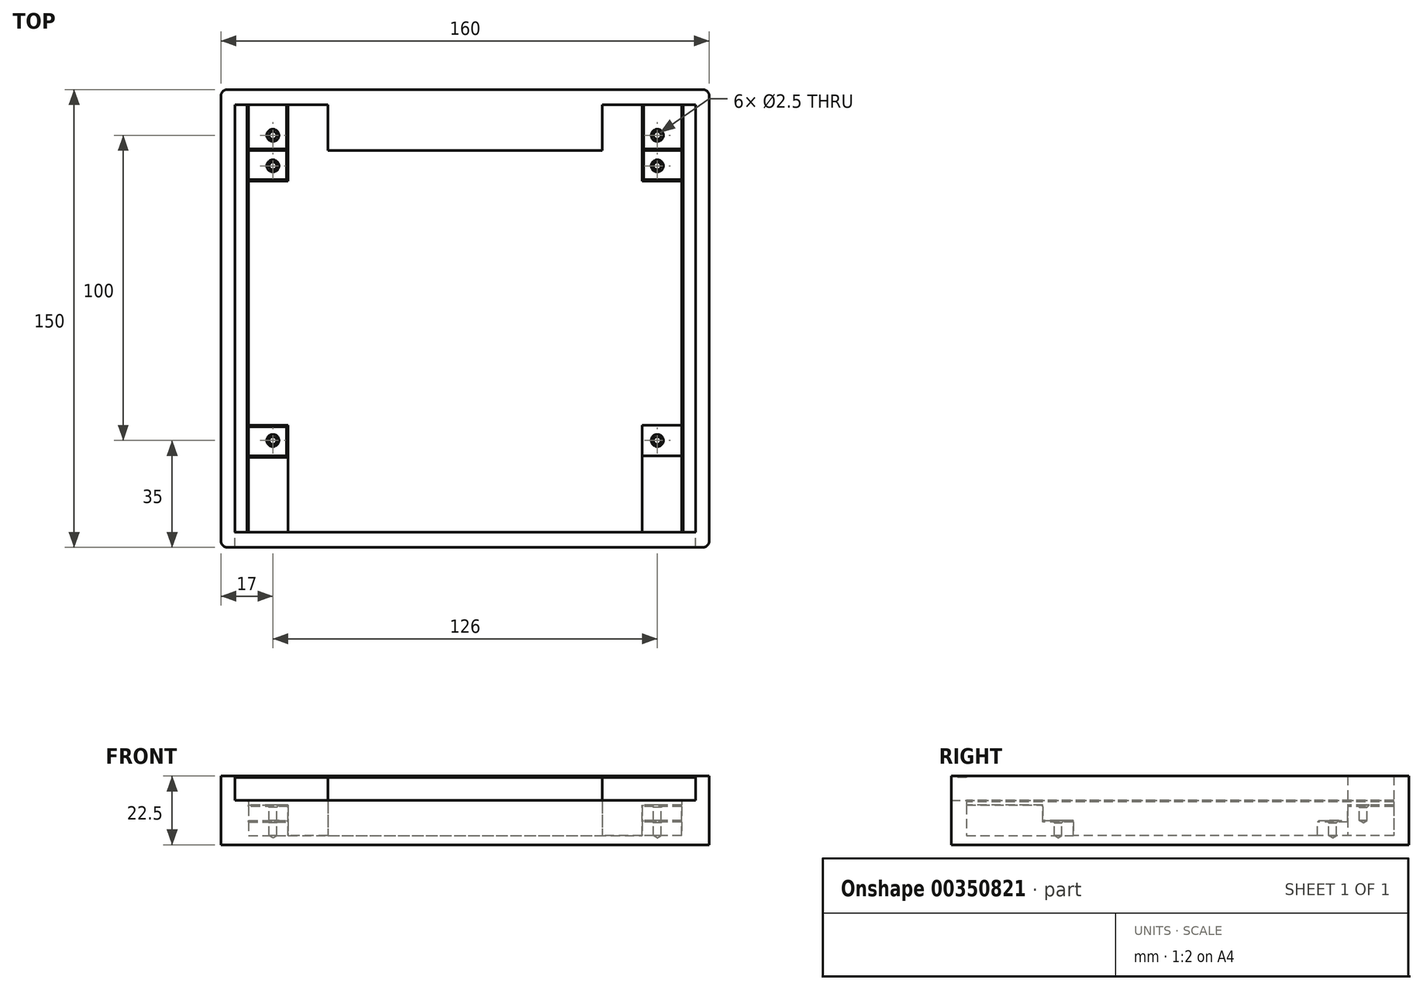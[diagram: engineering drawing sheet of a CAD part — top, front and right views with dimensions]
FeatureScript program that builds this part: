
annotation { "Feature Type Name" : "Feature", "Feature Type Description" : "" }
export const myFeature = defineFeature(function(context is Context, id is Id, definition is map)
    precondition{}
    {
        {
            var Q0;
            Q0=qCreatedBy(makeId("Top.planeOp"),FACE);
            var sketch = newSketch(context, id + "F0", { "sketchPlane" : qUnion([Q0])});
            skLineSegment(sketch, "E0.bottom", {"start": v(78, -75) * mm, "end": v(-78, -75) * mm});
            skLineSegment(sketch, "E0.top", {"start": v(78, 75) * mm, "end": v(-78, 75) * mm});
            skLineSegment(sketch, "E0.left", {"start": v(80, -73) * mm, "end": v(80, 73) * mm});
            skLineSegment(sketch, "E0.right", {"start": v(-80, -73) * mm, "end": v(-80, 73) * mm});
            skPoint(sketch, "E0.middle", {"position": v(0, 0) * mm});
            skPoint(sketch, "E1.visualSharp", {"position": v(-80, 75) * mm});
            skArc(sketch, "E1.filletArc", {"start": v(-78, 75) * mm, "mid": v(-79.41, 74.41) * mm, "end": v(-80, 73) * mm});
            skPoint(sketch, "E2.visualSharp", {"position": v(80, 75) * mm});
            skArc(sketch, "E2.filletArc", {"start": v(80, 73) * mm, "mid": v(79.41, 74.41) * mm, "end": v(78, 75) * mm});
            skPoint(sketch, "E3.visualSharp", {"position": v(80, -75) * mm});
            skArc(sketch, "E3.filletArc", {"start": v(78, -75) * mm, "mid": v(79.41, -74.41) * mm, "end": v(80, -73) * mm});
            skPoint(sketch, "E4.visualSharp", {"position": v(-80, -75) * mm});
            skArc(sketch, "E4.filletArc", {"start": v(-80, -73) * mm, "mid": v(-79.41, -74.41) * mm, "end": v(-78, -75) * mm});
            skSolve(sketch);
        }
        {
            var Q0;
            Q0 = qSketchRegion(id + "F0", true);
            extrude(context, id + "F1", {"entities" : qUnion([Q0]), "depth" : 3 * mm});
        }
        {
            var Q0;
            Q0=makeQuery(id+"F1.opExtrude","CAP_FACE",FACE,{"disambiguationData":[OSD([sQuery(id+"F0.wireOp",EDGE,"E0.bottom"),sQuery(id+"F0.wireOp",EDGE,"E0.top"),sQuery(id+"F0.wireOp",EDGE,"E0.left"),sQuery(id+"F0.wireOp",EDGE,"E0.right"),sQuery(id+"F0.wireOp",EDGE,"E1.filletArc"),sQuery(id+"F0.wireOp",EDGE,"E2.filletArc"),sQuery(id+"F0.wireOp",EDGE,"E3.filletArc"),sQuery(id+"F0.wireOp",EDGE,"E4.filletArc")])],"isStart":false});
            var sketch = newSketch(context, id + "F2", { "sketchPlane" : qUnion([Q0])});
            skLineSegment(sketch, "E5", {"start": v(15.36, 0) * mm, "end": v(-11.97, 0) * mm, "construction": true});
            skLineSegment(sketch, "E6", {"start": v(0, -7.28) * mm, "end": v(0, 8.54) * mm, "construction": true});
            skLineSegment(sketch, "E7.bottom", {"start": v(-68, -45) * mm, "end": v(-58, -45) * mm});
            skLineSegment(sketch, "E7.top", {"start": v(-68, -35) * mm, "end": v(-58, -35) * mm});
            skLineSegment(sketch, "E7.left", {"start": v(-68, -45) * mm, "end": v(-68, -35) * mm});
            skLineSegment(sketch, "E7.right", {"start": v(-58, -45) * mm, "end": v(-58, -35) * mm});
            skLineSegment(sketch, "E8.bottom", {"start": v(-68, 55) * mm, "end": v(-58, 55) * mm});
            skLineSegment(sketch, "E8.top", {"start": v(-68, 45) * mm, "end": v(-58, 45) * mm});
            skLineSegment(sketch, "E8.left", {"start": v(-68, 55) * mm, "end": v(-68, 45) * mm});
            skLineSegment(sketch, "E8.right", {"start": v(-58, 55) * mm, "end": v(-58, 45) * mm});
            skLineSegment(sketch, "E9.MirrorCS", {"start": v(68, 55) * mm, "end": v(68, 45) * mm});
            skLineSegment(sketch, "E10.MirrorCS", {"start": v(58, -45) * mm, "end": v(58, -35) * mm});
            skLineSegment(sketch, "E11.MirrorCS", {"start": v(68, -35) * mm, "end": v(58, -35) * mm});
            skLineSegment(sketch, "E12.MirrorCS", {"start": v(58, 55) * mm, "end": v(58, 45) * mm});
            skLineSegment(sketch, "E13.MirrorCS", {"start": v(68, -45) * mm, "end": v(68, -35) * mm});
            skLineSegment(sketch, "E14.MirrorCS", {"start": v(68, 55) * mm, "end": v(58, 55) * mm});
            skLineSegment(sketch, "E15.MirrorCS", {"start": v(68, 45) * mm, "end": v(58, 45) * mm});
            skLineSegment(sketch, "E16.MirrorCS", {"start": v(68, -45) * mm, "end": v(58, -45) * mm});
            skSolve(sketch);
        }
        {
            var Q0;
            Q0 = qSketchRegion(id + "F2", true);
            extrude(context, id + "F3", {"entities" : qUnion([Q0]), "operationType" : NewBodyOperationType.ADD, "depth" : 5 * mm});
        }
        {
            var Q0;
            Q0=makeQuery(id+"F3.opExtrude","CAP_FACE",FACE,{"disambiguationData":[OSD([sQuery(id+"F2.wireOp",EDGE,"E8.bottom"),sQuery(id+"F2.wireOp",EDGE,"E8.top"),sQuery(id+"F2.wireOp",EDGE,"E8.left"),sQuery(id+"F2.wireOp",EDGE,"E8.right")])],"isStart":false});
            var sketch = newSketch(context, id + "F4", { "sketchPlane" : qUnion([Q0])});
            skLineSegment(sketch, "E17", {"start": v(0, 12.76) * mm, "end": v(0, -16.1) * mm, "construction": true});
            skLineSegment(sketch, "E18", {"start": v(-10.9, 0) * mm, "end": v(16.66, 0) * mm, "construction": true});
            skPoint(sketch, "E19", {"position": v(-63, 50) * mm});
            skPoint(sketch, "E19.positionSnap0", {"position": v(-63, 55) * mm});
            skPoint(sketch, "E19.positionSnap1", {"position": v(-58, 50) * mm});
            skPoint(sketch, "E20", {"position": v(-63, -40) * mm});
            skPoint(sketch, "E21.MirrorP", {"position": v(63, -40) * mm});
            skPoint(sketch, "E22.MirrorP", {"position": v(58, 50) * mm});
            skPoint(sketch, "E23.MirrorP", {"position": v(63, 50) * mm});
            skSolve(sketch);
        }
        {
            var Q0;
            Q0=makeQuery(id+"F1.opExtrude","CAP_FACE",FACE,{"disambiguationData":[OSD([sQuery(id+"F0.wireOp",EDGE,"E0.bottom"),sQuery(id+"F0.wireOp",EDGE,"E0.top"),sQuery(id+"F0.wireOp",EDGE,"E0.left"),sQuery(id+"F0.wireOp",EDGE,"E0.right"),sQuery(id+"F0.wireOp",EDGE,"E1.filletArc"),sQuery(id+"F0.wireOp",EDGE,"E2.filletArc"),sQuery(id+"F0.wireOp",EDGE,"E3.filletArc"),sQuery(id+"F0.wireOp",EDGE,"E4.filletArc")])],"isStart":false});
            var sketch = newSketch(context, id + "F5", { "sketchPlane" : qUnion([Q0])});
            skLineSegment(sketch, "E24.bottom", {"start": v(-68, 55) * mm, "end": v(-58, 55) * mm});
            skLineSegment(sketch, "E24.top", {"start": v(-68, 65) * mm, "end": v(-58, 65) * mm});
            skLineSegment(sketch, "E24.left", {"start": v(-68, 55) * mm, "end": v(-68, 65) * mm});
            skLineSegment(sketch, "E24.right", {"start": v(-58, 55) * mm, "end": v(-58, 65) * mm});
            skLineSegment(sketch, "E25", {"start": v(0, -3.53) * mm, "end": v(0, 31.26) * mm, "construction": true});
            skLineSegment(sketch, "E26", {"start": v(-9.48, 0) * mm, "end": v(18.02, 0) * mm, "construction": true});
            skLineSegment(sketch, "E27.bottom", {"start": v(-68, -45) * mm, "end": v(-58, -45) * mm});
            skLineSegment(sketch, "E27.top", {"start": v(-68, -55) * mm, "end": v(-58, -55) * mm});
            skLineSegment(sketch, "E27.left", {"start": v(-68, -45) * mm, "end": v(-68, -55) * mm});
            skLineSegment(sketch, "E27.right", {"start": v(-58, -45) * mm, "end": v(-58, -55) * mm});
            skLineSegment(sketch, "E28.MirrorCS", {"start": v(68, 55) * mm, "end": v(58, 55) * mm});
            skLineSegment(sketch, "E29.MirrorCS", {"start": v(68, 65) * mm, "end": v(58, 65) * mm});
            skLineSegment(sketch, "E30.MirrorCS", {"start": v(68, -55) * mm, "end": v(58, -55) * mm});
            skLineSegment(sketch, "E31.MirrorCS", {"start": v(58, 55) * mm, "end": v(58, 65) * mm});
            skLineSegment(sketch, "E32.MirrorCS", {"start": v(58, -45) * mm, "end": v(58, -55) * mm});
            skLineSegment(sketch, "E33.MirrorCS", {"start": v(68, -45) * mm, "end": v(68, -55) * mm});
            skLineSegment(sketch, "E34.MirrorCS", {"start": v(68, -45) * mm, "end": v(58, -45) * mm});
            skLineSegment(sketch, "E35.MirrorCS", {"start": v(68, 55) * mm, "end": v(68, 65) * mm});
            skSolve(sketch);
        }
        {
            var Q0;
            Q0 = qSketchRegion(id + "F5", true);
            extrude(context, id + "F6", {"entities" : qUnion([Q0]), "operationType" : NewBodyOperationType.ADD, "depth" : 10 * mm});
        }
        {
            var Q0;
            Q0=makeQuery(id+"F6.opExtrude","CAP_FACE",FACE,{"disambiguationData":[OSD([sQuery(id+"F5.wireOp",EDGE,"E24.bottom"),sQuery(id+"F5.wireOp",EDGE,"E24.top"),sQuery(id+"F5.wireOp",EDGE,"E24.left"),sQuery(id+"F5.wireOp",EDGE,"E24.right")])],"isStart":false});
            var sketch = newSketch(context, id + "F7", { "sketchPlane" : qUnion([Q0])});
            skPoint(sketch, "E36", {"position": v(-63, 60) * mm});
            skPoint(sketch, "E36.positionSnap0", {"position": v(-58, 60) * mm});
            skPoint(sketch, "E37", {"position": v(63, 60) * mm});
            skSolve(sketch);
        }
        {
            var Q0;
            Q0=sQuery(id+"F4.wireOp",VERTEX,"dee3a072-0559-4f3e-aa8e-34885224e21b");
            var Q1;
            Q1=sQuery(id+"F4.wireOp",VERTEX,"d39e51ca-cc14-4291-bc97-98dbb002058f0.MirrorP");
            var Q2;
            Q2=sQuery(id+"F4.wireOp",VERTEX,"d39e51ca-cc14-4291-bc97-98dbb002058f1.MirrorP");
            var Q3;
            Q3=sQuery(id+"F4.wireOp",VERTEX,"049a6676-49f8-4cd7-b6db-b765b2aac7f50.MirrorP");
            var Q4;
            Q4=sQuery(id+"F7.wireOp",VERTEX,"E36");
            var Q5;
            Q5=sQuery(id+"F7.wireOp",VERTEX,"E37");
            var Q6;
            Q6=sQuery(id+"F4.wireOp",VERTEX,"E20");
            var Q7;
            Q7=sQuery(id+"F4.wireOp",VERTEX,"E21.MirrorP");
            var Q8;
            Q8=sQuery(id+"F4.wireOp",VERTEX,"E19");
            var Q9;
            Q9=sQuery(id+"F4.wireOp",VERTEX,"E23.MirrorP");
            var Q10;
            Q10=makeQuery(id+"F1.opExtrude","SWEPT_BODY",BODY,{"disambiguationData":[OSD([sQuery(id+"F0.wireOp",EDGE,"E0.bottom"),sQuery(id+"F0.wireOp",EDGE,"E0.top"),sQuery(id+"F0.wireOp",EDGE,"E0.left"),sQuery(id+"F0.wireOp",EDGE,"E0.right"),sQuery(id+"F0.wireOp",EDGE,"E1.filletArc"),sQuery(id+"F0.wireOp",EDGE,"E2.filletArc"),sQuery(id+"F0.wireOp",EDGE,"E3.filletArc"),sQuery(id+"F0.wireOp",EDGE,"E4.filletArc")])]});
            hole(context, id + "F8", {"style" : HoleStyle.C_SINK, "endStyle" : HoleEndStyle.BLIND, "holeDiameter" : 2.5 * mm, "cSinkDiameter" : 4 * mm, "cSinkAngle" : 90 * degree, "holeDepth" : 5 * mm, "isTappedThrough" : true, "tappedDepth" : 5 * mm, "tapClearance" : 3, "locations" : qUnion([Q0, Q1, Q2, Q3, Q4, Q5, Q6, Q7, Q8, Q9]), "scope" : qUnion([Q10])});
        }
        {
            var Q0;
            Q0=makeQuery(id+"F1.opExtrude","CAP_FACE",FACE,{"disambiguationData":[OSD([sQuery(id+"F0.wireOp",EDGE,"E0.bottom"),sQuery(id+"F0.wireOp",EDGE,"E0.top"),sQuery(id+"F0.wireOp",EDGE,"E0.left"),sQuery(id+"F0.wireOp",EDGE,"E0.right"),sQuery(id+"F0.wireOp",EDGE,"E1.filletArc"),sQuery(id+"F0.wireOp",EDGE,"E2.filletArc"),sQuery(id+"F0.wireOp",EDGE,"E3.filletArc"),sQuery(id+"F0.wireOp",EDGE,"E4.filletArc")])],"isStart":false});
            var sketch = newSketch(context, id + "F9", { "sketchPlane" : qUnion([Q0])});
            skLineSegment(sketch, "E38.top", {"start": v(-71, -70) * mm, "end": v(-80, -70) * mm});
            skLineSegment(sketch, "E38.left", {"start": v(-71, 70) * mm, "end": v(-71, -70) * mm});
            skLineSegment(sketch, "E38.right", {"start": v(-80, 70) * mm, "end": v(-80, -70) * mm});
            skLineSegment(sketch, "E39", {"start": v(0, -8.37) * mm, "end": v(0, 11.77) * mm, "construction": true});
            skLineSegment(sketch, "E40.MirrorCS", {"start": v(80, 70) * mm, "end": v(80, -70) * mm});
            skLineSegment(sketch, "E41.MirrorCS", {"start": v(71, 70) * mm, "end": v(71, -70) * mm});
            skLineSegment(sketch, "E42.MirrorCS", {"start": v(71, -70) * mm, "end": v(80, -70) * mm});
            skLineSegment(sketch, "E43", {"start": v(-80, 70) * mm, "end": v(-71, 70) * mm});
            skLineSegment(sketch, "E44", {"start": v(71, 70) * mm, "end": v(80, 70) * mm});
            skSolve(sketch);
        }
        {
            var Q0;
            Q0 = qSketchRegion(id + "F9", true);
            extrude(context, id + "F10", {"entities" : qUnion([Q0]), "operationType" : NewBodyOperationType.ADD, "depth" : 11.5 * mm});
        }
        {
            var Q0;
            Q0=makeQuery(id+"F10.opExtrude","CAP_FACE",FACE,{"disambiguationData":[OSD([sQuery(id+"F9.wireOp",EDGE,"E38.bottom"),sQuery(id+"F9.wireOp",EDGE,"E38.top"),sQuery(id+"F9.wireOp",EDGE,"E38.left"),sQuery(id+"F9.wireOp",EDGE,"E38.right")])],"isStart":false});
            var sketch = newSketch(context, id + "F11", { "sketchPlane" : qUnion([Q0])});
            skLineSegment(sketch, "E45.bottom", {"start": v(-80, -70) * mm, "end": v(-75.5, -70) * mm});
            skLineSegment(sketch, "E45.top", {"start": v(-80, -70) * mm, "end": v(-75.5, -70) * mm});
            skLineSegment(sketch, "E45.left", {"start": v(-80, -70) * mm, "end": v(-80, -70) * mm});
            skLineSegment(sketch, "E45.right", {"start": v(-75.5, -70) * mm, "end": v(-75.5, -70) * mm});
            skLineSegment(sketch, "E46", {"start": v(0, -3.83) * mm, "end": v(0, 7.5) * mm, "construction": true});
            skLineSegment(sketch, "E47.MirrorCS", {"start": v(75.5, -70) * mm, "end": v(75.5, -70) * mm});
            skLineSegment(sketch, "E48.MirrorCS", {"start": v(80, -70) * mm, "end": v(80, -70) * mm});
            skLineSegment(sketch, "E49.MirrorCS", {"start": v(80, -70) * mm, "end": v(75.5, -70) * mm});
            skLineSegment(sketch, "E50", {"start": v(-75.5, -70) * mm, "end": v(-75.5, 70) * mm});
            skLineSegment(sketch, "E51", {"start": v(-75.5, 70) * mm, "end": v(-80, 70) * mm});
            skLineSegment(sketch, "E52", {"start": v(-80, 70) * mm, "end": v(-80, -70) * mm});
            skLineSegment(sketch, "E53.MirrorCS", {"start": v(75.5, 70) * mm, "end": v(80, 70) * mm});
            skLineSegment(sketch, "E54.MirrorCS", {"start": v(75.5, -70) * mm, "end": v(75.5, 70) * mm});
            skLineSegment(sketch, "E55.0", {"start": v(80, -70) * mm, "end": v(80, 70) * mm});
            skSolve(sketch);
        }
        {
            var Q0;
            Q0 = qSketchRegion(id + "F11", true);
            extrude(context, id + "F12", {"entities" : qUnion([Q0]), "operationType" : NewBodyOperationType.ADD, "depth" : 8 * mm});
        }
        {
            var Q0;
            Q0=makeQuery(id+"F1.opExtrude","CAP_FACE",FACE,{"disambiguationData":[OSD([sQuery(id+"F0.wireOp",EDGE,"E0.bottom"),sQuery(id+"F0.wireOp",EDGE,"E0.top"),sQuery(id+"F0.wireOp",EDGE,"E0.left"),sQuery(id+"F0.wireOp",EDGE,"E0.right"),sQuery(id+"F0.wireOp",EDGE,"E1.filletArc"),sQuery(id+"F0.wireOp",EDGE,"E2.filletArc"),sQuery(id+"F0.wireOp",EDGE,"E3.filletArc"),sQuery(id+"F0.wireOp",EDGE,"E4.filletArc")])],"isStart":false});
            var sketch = newSketch(context, id + "F13", { "sketchPlane" : qUnion([Q0])});
            skLineSegment(sketch, "E56.0", {"start": v(-80, -73) * mm, "end": v(-80, -70) * mm});
            skArc(sketch, "E56.1", {"start": v(-80, -73) * mm, "mid": v(-79.41, -74.41) * mm, "end": v(-78, -75) * mm});
            skLineSegment(sketch, "E56.2", {"start": v(78, -75) * mm, "end": v(-78, -75) * mm});
            skArc(sketch, "E56.3", {"start": v(78, -75) * mm, "mid": v(79.41, -74.41) * mm, "end": v(80, -73) * mm});
            skLineSegment(sketch, "E56.4", {"start": v(80, -73) * mm, "end": v(80, -70) * mm});
            skLineSegment(sketch, "E57", {"start": v(-80, -70) * mm, "end": v(80, -70) * mm});
            skLineSegment(sketch, "E58.0", {"start": v(-80, 70) * mm, "end": v(-80, 73) * mm});
            skArc(sketch, "E58.1", {"start": v(-78, 75) * mm, "mid": v(-79.41, 74.41) * mm, "end": v(-80, 73) * mm});
            skLineSegment(sketch, "E58.2", {"start": v(78, 75) * mm, "end": v(-78, 75) * mm});
            skArc(sketch, "E58.3", {"start": v(80, 73) * mm, "mid": v(79.41, 74.41) * mm, "end": v(78, 75) * mm});
            skLineSegment(sketch, "E58.4", {"start": v(80, 70) * mm, "end": v(80, 73) * mm});
            skLineSegment(sketch, "E59", {"start": v(80, 70) * mm, "end": v(-80, 70) * mm});
            skSolve(sketch);
        }
        {
            var Q0;
            Q0 = qSketchRegion(id + "F13", true);
            var Q1;
            Q1=makeQuery(id+"F12.opExtrude","CAP_FACE",FACE,{"disambiguationData":[OSD([sQuery(id+"F11.wireOp",EDGE,"E45.bottom"),sQuery(id+"F11.wireOp",EDGE,"E45.top"),sQuery(id+"F11.wireOp",EDGE,"E45.left"),sQuery(id+"F11.wireOp",EDGE,"E45.right")])],"isStart":false});
            extrude(context, id + "F14", {"entities" : qUnion([Q0]), "operationType" : NewBodyOperationType.ADD, "endBound" : BoundingType.UP_TO_SURFACE, "endBoundEntityFace" : qUnion([Q1]), "depth" : 25 * mm});
        }
        {
            var Q0;
            Q0=makeQuery(id+"F14.boolean.opBoolean","MERGE",FACE,{"derivedFrom":[makeQuery(id+"F1.opExtrude","SWEPT_FACE",FACE,{"disambiguationData":[OSD([sQuery(id+"F0.wireOp",EDGE,"E0.bottom")])]}),makeQuery(id+"F14.opExtrude","SWEPT_FACE",FACE,{"disambiguationData":[OSD([sQuery(id+"F13.wireOp",EDGE,"E56.2")])]})]});
            var sketch = newSketch(context, id + "F15", { "sketchPlane" : qUnion([Q0])});
            skLineSegment(sketch, "E60.0", {"start": v(-75.5, 22) * mm, "end": v(-75.5, 14.5) * mm});
            skLineSegment(sketch, "E60.5", {"start": v(75.5, 22.5) * mm, "end": v(75.5, 14.5) * mm});
            skLineSegment(sketch, "E61", {"start": v(-75.5, 22) * mm, "end": v(75.5, 22) * mm});
            skPoint(sketch, "E62.orphan", {"position": v(-75.5, 22.5) * mm});
            skLineSegment(sketch, "E63.0", {"start": v(75.5, 14.5) * mm, "end": v(-75.5, 14.5) * mm});
            skSolve(sketch);
        }
        {
            var Q0;
            Q0 = qSketchRegion(id + "F15", true);
            extrude(context, id + "F16", {"entities" : qUnion([Q0]), "operationType" : NewBodyOperationType.REMOVE, "endBound" : BoundingType.UP_TO_NEXT, "oppositeDirection" : true, "depth" : 25 * mm});
        }
        {
            var Q0;
            Q0=makeQuery(id+"F6.boolean.opBoolean","MERGE",FACE,{"derivedFrom":[makeQuery(id+"F3.opExtrude","SWEPT_FACE",FACE,{"disambiguationData":[OSD([sQuery(id+"F2.wireOp",EDGE,"E8.left")])]}),makeQuery(id+"F6.opExtrude","SWEPT_FACE",FACE,{"disambiguationData":[OSD([sQuery(id+"F5.wireOp",EDGE,"E24.left")])]})]});
            var sketch = newSketch(context, id + "F17", { "sketchPlane" : qUnion([Q0])});
            skLineSegment(sketch, "E64.0.0", {"start": v(-45, 3) * mm, "end": v(-65, 3) * mm});
            skLineSegment(sketch, "E64.0.1", {"start": v(-65, 3) * mm, "end": v(-65, 13) * mm});
            skLineSegment(sketch, "E64.0.2", {"start": v(-65, 13) * mm, "end": v(-55, 13) * mm});
            skLineSegment(sketch, "E64.0.3", {"start": v(-55, 13) * mm, "end": v(-55, 8) * mm});
            skLineSegment(sketch, "E64.0.4", {"start": v(-55, 8) * mm, "end": v(-45, 8) * mm});
            skLineSegment(sketch, "E64.0.5", {"start": v(-45, 8) * mm, "end": v(-45, 3) * mm});
            skLineSegment(sketch, "E65.0.0", {"start": v(55, 3) * mm, "end": v(35, 3) * mm});
            skLineSegment(sketch, "E65.0.1", {"start": v(35, 3) * mm, "end": v(35, 8) * mm});
            skLineSegment(sketch, "E65.0.2", {"start": v(35, 8) * mm, "end": v(45, 8) * mm});
            skLineSegment(sketch, "E65.0.3", {"start": v(45, 8) * mm, "end": v(45, 13) * mm});
            skLineSegment(sketch, "E65.0.4", {"start": v(45, 13) * mm, "end": v(55, 13) * mm});
            skLineSegment(sketch, "E65.0.5", {"start": v(55, 13) * mm, "end": v(55, 3) * mm});
            skSolve(sketch);
        }
        {
            var Q0;
            Q0 = qSketchRegion(id + "F17", true);
            extrude(context, id + "F18", {"entities" : qUnion([Q0]), "operationType" : NewBodyOperationType.ADD, "endBound" : BoundingType.UP_TO_NEXT, "depth" : 25 * mm});
        }
        {
            var Q0;
            Q0=makeQuery(id+"F18.boolean.opBoolean","MERGE",FACE,{"derivedFrom":[makeQuery(id+"F6.opExtrude","SWEPT_FACE",FACE,{"disambiguationData":[OSD([sQuery(id+"F5.wireOp",EDGE,"E24.top")])]}),makeQuery(id+"F18.opExtrude","SWEPT_FACE",FACE,{"disambiguationData":[OSD([sQuery(id+"F17.wireOp",EDGE,"E64.0.1")])]})]});
            var sketch = newSketch(context, id + "F19", { "sketchPlane" : qUnion([Q0])});
            skLineSegment(sketch, "E66.0.0", {"start": v(58, 3) * mm, "end": v(71, 3) * mm});
            skLineSegment(sketch, "E66.0.1", {"start": v(71, 3) * mm, "end": v(71, 13) * mm});
            skLineSegment(sketch, "E66.0.2", {"start": v(71, 13) * mm, "end": v(58, 13) * mm});
            skLineSegment(sketch, "E66.0.3", {"start": v(58, 13) * mm, "end": v(58, 3) * mm});
            skLineSegment(sketch, "E67.0.0", {"start": v(-68, 3) * mm, "end": v(-58, 3) * mm});
            skLineSegment(sketch, "E67.0.1", {"start": v(-58, 3) * mm, "end": v(-58, 13) * mm});
            skLineSegment(sketch, "E67.0.2", {"start": v(-58, 13) * mm, "end": v(-68, 13) * mm});
            skLineSegment(sketch, "E67.0.3", {"start": v(-68, 13) * mm, "end": v(-68, 3) * mm});
            skSolve(sketch);
        }
        {
            var Q0;
            Q0 = qSketchRegion(id + "F19", true);
            extrude(context, id + "F20", {"entities" : qUnion([Q0]), "operationType" : NewBodyOperationType.ADD, "endBound" : BoundingType.UP_TO_NEXT, "depth" : 25 * mm});
        }
        {
            var Q0;
            Q0=makeQuery(id+"F20.boolean.opBoolean","MERGE",FACE,{"derivedFrom":[makeQuery(id+"F6.boolean.opBoolean","MERGE",FACE,{"derivedFrom":[makeQuery(id+"F3.opExtrude","SWEPT_FACE",FACE,{"disambiguationData":[OSD([sQuery(id+"F2.wireOp",EDGE,"E9.MirrorCS")])]}),makeQuery(id+"F6.opExtrude","SWEPT_FACE",FACE,{"disambiguationData":[OSD([sQuery(id+"F5.wireOp",EDGE,"E35.MirrorCS")])]})]}),makeQuery(id+"F20.opExtrude","SWEPT_FACE",FACE,{"disambiguationData":[OSD([sQuery(id+"F19.wireOp",EDGE,"E67.0.3")])]})]});
            var sketch = newSketch(context, id + "F21", { "sketchPlane" : qUnion([Q0])});
            skLineSegment(sketch, "E68.0.0", {"start": v(45, 3) * mm, "end": v(70, 3) * mm});
            skLineSegment(sketch, "E68.0.1", {"start": v(70, 3) * mm, "end": v(70, 13) * mm});
            skLineSegment(sketch, "E68.0.2", {"start": v(70, 13) * mm, "end": v(55, 13) * mm});
            skLineSegment(sketch, "E68.0.3", {"start": v(55, 13) * mm, "end": v(55, 8) * mm});
            skLineSegment(sketch, "E68.0.4", {"start": v(55, 8) * mm, "end": v(45, 8) * mm});
            skLineSegment(sketch, "E68.0.5", {"start": v(45, 8) * mm, "end": v(45, 3) * mm});
            skLineSegment(sketch, "E69.0.0", {"start": v(-55, 3) * mm, "end": v(-35, 3) * mm});
            skLineSegment(sketch, "E69.0.1", {"start": v(-35, 3) * mm, "end": v(-35, 8) * mm});
            skLineSegment(sketch, "E69.0.2", {"start": v(-35, 8) * mm, "end": v(-45, 8) * mm});
            skLineSegment(sketch, "E69.0.3", {"start": v(-45, 8) * mm, "end": v(-45, 13) * mm});
            skLineSegment(sketch, "E69.0.4", {"start": v(-45, 13) * mm, "end": v(-55, 13) * mm});
            skLineSegment(sketch, "E69.0.5", {"start": v(-55, 13) * mm, "end": v(-55, 3) * mm});
            skSolve(sketch);
        }
        {
            var Q0;
            Q0 = qSketchRegion(id + "F21", true);
            extrude(context, id + "F22", {"entities" : qUnion([Q0]), "operationType" : NewBodyOperationType.ADD, "endBound" : BoundingType.UP_TO_NEXT, "depth" : 25 * mm});
        }
        {
            var Q0;
            Q0=makeQuery(id+"F22.boolean.opBoolean","MERGE",FACE,{"derivedFrom":[makeQuery(id+"F6.opExtrude","SWEPT_FACE",FACE,{"disambiguationData":[OSD([sQuery(id+"F5.wireOp",EDGE,"E30.MirrorCS")])]}),makeQuery(id+"F22.opExtrude","SWEPT_FACE",FACE,{"disambiguationData":[OSD([sQuery(id+"F21.wireOp",EDGE,"E69.0.5")])]})]});
            var sketch = newSketch(context, id + "F23", { "sketchPlane" : qUnion([Q0])});
            skLineSegment(sketch, "E70.0.0", {"start": v(58, 3) * mm, "end": v(71, 3) * mm});
            skLineSegment(sketch, "E70.0.1", {"start": v(71, 3) * mm, "end": v(71, 13) * mm});
            skLineSegment(sketch, "E70.0.2", {"start": v(71, 13) * mm, "end": v(58, 13) * mm});
            skLineSegment(sketch, "E70.0.3", {"start": v(58, 13) * mm, "end": v(58, 3) * mm});
            skLineSegment(sketch, "E71.0.0", {"start": v(-71, 3) * mm, "end": v(-58, 3) * mm});
            skLineSegment(sketch, "E71.0.1", {"start": v(-58, 3) * mm, "end": v(-58, 13) * mm});
            skLineSegment(sketch, "E71.0.2", {"start": v(-58, 13) * mm, "end": v(-71, 13) * mm});
            skLineSegment(sketch, "E71.0.3", {"start": v(-71, 13) * mm, "end": v(-71, 3) * mm});
            skSolve(sketch);
        }
        {
            var Q0;
            Q0 = qSketchRegion(id + "F23", true);
            extrude(context, id + "F24", {"entities" : qUnion([Q0]), "operationType" : NewBodyOperationType.ADD, "endBound" : BoundingType.UP_TO_NEXT, "depth" : 25 * mm});
        }
        {
            var Q0;
            Q0=makeQuery(id+"F1.opExtrude","CAP_FACE",FACE,{"disambiguationData":[OSD([sQuery(id+"F0.wireOp",EDGE,"E0.bottom"),sQuery(id+"F0.wireOp",EDGE,"E0.top"),sQuery(id+"F0.wireOp",EDGE,"E0.left"),sQuery(id+"F0.wireOp",EDGE,"E0.right"),sQuery(id+"F0.wireOp",EDGE,"E1.filletArc"),sQuery(id+"F0.wireOp",EDGE,"E2.filletArc"),sQuery(id+"F0.wireOp",EDGE,"E3.filletArc"),sQuery(id+"F0.wireOp",EDGE,"E4.filletArc")])],"isStart":false});
            var sketch = newSketch(context, id + "F25", { "sketchPlane" : qUnion([Q0])});
            skLineSegment(sketch, "E72.bottom", {"start": v(-45, 70) * mm, "end": v(45, 70) * mm});
            skLineSegment(sketch, "E72.top", {"start": v(-45, 55) * mm, "end": v(45, 55) * mm});
            skLineSegment(sketch, "E72.left", {"start": v(-45, 70) * mm, "end": v(-45, 55) * mm});
            skLineSegment(sketch, "E72.right", {"start": v(45, 70) * mm, "end": v(45, 55) * mm});
            skSolve(sketch);
        }
        {
            var Q0;
            Q0 = qSketchRegion(id + "F25", true);
            var Q1;
            {var subQ0=sQuery(id+"F11.wireOp",EDGE,"E52");var subQ1=sQuery(id+"F11.wireOp",EDGE,"E51");var subQ2=sQuery(id+"F11.wireOp",EDGE,"E50");var subQ3=sQuery(id+"F11.wireOp",EDGE,"E45.top");Q1=makeQuery(id+"F14.boolean.opBoolean","MERGE",FACE,{"derivedFrom":[makeQuery(id+"F12.opExtrude","CAP_FACE",FACE,{"disambiguationData":[OSD([subQ3,subQ2,subQ1,subQ0])],"isStart":false}),makeQuery(id+"F12.opExtrude","CAP_FACE",FACE,{"disambiguationData":[OSD([sQuery(id+"F11.wireOp",EDGE,"E53.MirrorCS"),sQuery(id+"F11.wireOp",EDGE,"E54.MirrorCS"),sQuery(id+"F11.wireOp",EDGE,"E49.MirrorCS"),sQuery(id+"F11.wireOp",EDGE,"E55.0")])],"isStart":false}),makeQuery(id+"F14.opExtrude","CAP_FACE",FACE,{"disambiguationData":[OSD([subQ3,subQ2,subQ1,subQ0]),ownerDisambiguation([makeQuery(id+"F13.imprint","IMPRINT",EDGE,{"derivedFrom":sQuery(id+"F13.wireOp",EDGE,"E56.0")})])],"isStart":false}),makeQuery(id+"F14.opExtrude","CAP_FACE",FACE,{"disambiguationData":[OSD([subQ3,subQ2,subQ1,subQ0]),ownerDisambiguation([makeQuery(id+"F13.imprint","IMPRINT",EDGE,{"derivedFrom":sQuery(id+"F13.wireOp",EDGE,"E58.0")})])],"isStart":false})]});}
            extrude(context, id + "F26", {"entities" : qUnion([Q0]), "operationType" : NewBodyOperationType.ADD, "endBound" : BoundingType.UP_TO_SURFACE, "endBoundEntityFace" : qUnion([Q1]), "depth" : 25 * mm});
        }
        {
            var Q0;
            Q0=makeQuery(id+"F10.opExtrude","CAP_EDGE",EDGE,{"disambiguationData":[OSD([sQuery(id+"F9.wireOp",EDGE,"E41.MirrorCS")])],"isStart":false});
            var Q1;
            Q1=makeQuery(id+"F10.opExtrude","CAP_EDGE",EDGE,{"disambiguationData":[OSD([sQuery(id+"F9.wireOp",EDGE,"E38.left")])],"isStart":false});
            var Q2;
            {var subQ0=sQuery(id+"F5.wireOp",EDGE,"E24.right");Q2=makeQuery(id+"F20.boolean.opBoolean","MERGE",EDGE,{"derivedFrom":[makeQuery(id+"F6.opExtrude","CAP_EDGE",EDGE,{"disambiguationData":[OSD([subQ0])],"isStart":false}),makeQuery(id+"F20.opExtrude","SWEPT_EDGE",EDGE,{"disambiguationData":[OSD([sQuery(id+"F5.wireOp",EDGE,"E24.top"),subQ0,sQuery(id+"F19.wireOp",EDGE,"E66.0.2"),sQuery(id+"F19.wireOp",EDGE,"E66.0.3")])]})]});}
            var Q3;
            {var subQ0=sQuery(id+"F5.wireOp",EDGE,"E24.bottom");Q3=makeQuery(id+"F18.boolean.opBoolean","MERGE",EDGE,{"derivedFrom":[makeQuery(id+"F6.opExtrude","CAP_EDGE",EDGE,{"disambiguationData":[OSD([subQ0])],"isStart":false}),makeQuery(id+"F18.opExtrude","SWEPT_EDGE",EDGE,{"disambiguationData":[OSD([sQuery(id+"F2.wireOp",EDGE,"E8.left"),subQ0,sQuery(id+"F5.wireOp",EDGE,"E24.left"),sQuery(id+"F17.wireOp",EDGE,"E64.0.2"),sQuery(id+"F17.wireOp",EDGE,"E64.0.3")])]})]});}
            var Q4;
            Q4=makeQuery(id+"F3.opExtrude","CAP_EDGE",EDGE,{"disambiguationData":[OSD([sQuery(id+"F2.wireOp",EDGE,"E8.right")])],"isStart":false});
            var Q5;
            {var subQ0=sQuery(id+"F2.wireOp",EDGE,"E8.top");Q5=makeQuery(id+"F18.boolean.opBoolean","MERGE",EDGE,{"derivedFrom":[makeQuery(id+"F3.opExtrude","CAP_EDGE",EDGE,{"disambiguationData":[OSD([subQ0])],"isStart":false}),makeQuery(id+"F18.opExtrude","SWEPT_EDGE",EDGE,{"disambiguationData":[OSD([subQ0,sQuery(id+"F2.wireOp",EDGE,"E8.left"),sQuery(id+"F17.wireOp",EDGE,"E64.0.4"),sQuery(id+"F17.wireOp",EDGE,"E64.0.5")])]})]});}
            var Q6;
            {var subQ0=sQuery(id+"F5.wireOp",EDGE,"E27.bottom");Q6=makeQuery(id+"F18.boolean.opBoolean","MERGE",EDGE,{"derivedFrom":[makeQuery(id+"F6.opExtrude","CAP_EDGE",EDGE,{"disambiguationData":[OSD([subQ0])],"isStart":false}),makeQuery(id+"F18.opExtrude","SWEPT_EDGE",EDGE,{"disambiguationData":[OSD([sQuery(id+"F2.wireOp",EDGE,"E7.left"),subQ0,sQuery(id+"F5.wireOp",EDGE,"E27.left"),sQuery(id+"F17.wireOp",EDGE,"E65.0.3"),sQuery(id+"F17.wireOp",EDGE,"E65.0.4")])]})]});}
            var Q7;
            Q7=makeQuery(id+"F3.opExtrude","CAP_EDGE",EDGE,{"disambiguationData":[OSD([sQuery(id+"F2.wireOp",EDGE,"E7.right")])],"isStart":false});
            var Q8;
            {var subQ0=sQuery(id+"F2.wireOp",EDGE,"E7.top");Q8=makeQuery(id+"F18.boolean.opBoolean","MERGE",EDGE,{"derivedFrom":[makeQuery(id+"F3.opExtrude","CAP_EDGE",EDGE,{"disambiguationData":[OSD([subQ0])],"isStart":false}),makeQuery(id+"F18.opExtrude","SWEPT_EDGE",EDGE,{"disambiguationData":[OSD([subQ0,sQuery(id+"F2.wireOp",EDGE,"E7.left"),sQuery(id+"F17.wireOp",EDGE,"E65.0.1"),sQuery(id+"F17.wireOp",EDGE,"E65.0.2")])]})]});}
            var Q9;
            {var subQ0=sQuery(id+"F5.wireOp",EDGE,"E31.MirrorCS");Q9=makeQuery(id+"F20.boolean.opBoolean","MERGE",EDGE,{"derivedFrom":[makeQuery(id+"F6.opExtrude","CAP_EDGE",EDGE,{"disambiguationData":[OSD([subQ0])],"isStart":false}),makeQuery(id+"F20.opExtrude","SWEPT_EDGE",EDGE,{"disambiguationData":[OSD([sQuery(id+"F5.wireOp",EDGE,"E29.MirrorCS"),subQ0,sQuery(id+"F19.wireOp",EDGE,"E67.0.1"),sQuery(id+"F19.wireOp",EDGE,"E67.0.2")])]})]});}
            var Q10;
            {var subQ0=sQuery(id+"F5.wireOp",EDGE,"E28.MirrorCS");Q10=makeQuery(id+"F22.boolean.opBoolean","MERGE",EDGE,{"derivedFrom":[makeQuery(id+"F6.opExtrude","CAP_EDGE",EDGE,{"disambiguationData":[OSD([subQ0])],"isStart":false}),makeQuery(id+"F22.opExtrude","SWEPT_EDGE",EDGE,{"disambiguationData":[OSD([sQuery(id+"F2.wireOp",EDGE,"E9.MirrorCS"),subQ0,sQuery(id+"F5.wireOp",EDGE,"E35.MirrorCS"),sQuery(id+"F21.wireOp",EDGE,"E68.0.2"),sQuery(id+"F21.wireOp",EDGE,"E68.0.3")])]})]});}
            var Q11;
            Q11=makeQuery(id+"F3.opExtrude","CAP_EDGE",EDGE,{"disambiguationData":[OSD([sQuery(id+"F2.wireOp",EDGE,"E12.MirrorCS")])],"isStart":false});
            var Q12;
            {var subQ0=sQuery(id+"F2.wireOp",EDGE,"E15.MirrorCS");Q12=makeQuery(id+"F22.boolean.opBoolean","MERGE",EDGE,{"derivedFrom":[makeQuery(id+"F3.opExtrude","CAP_EDGE",EDGE,{"disambiguationData":[OSD([subQ0])],"isStart":false}),makeQuery(id+"F22.opExtrude","SWEPT_EDGE",EDGE,{"disambiguationData":[OSD([sQuery(id+"F2.wireOp",EDGE,"E9.MirrorCS"),subQ0,sQuery(id+"F21.wireOp",EDGE,"E68.0.4"),sQuery(id+"F21.wireOp",EDGE,"E68.0.5")])]})]});}
            var Q13;
            Q13=makeQuery(id+"F16.boolean.opBoolean","COPY",EDGE,{"derivedFrom":makeQuery(id+"F16.opExtrude","CAP_EDGE",EDGE,{"disambiguationData":[OSD([sQuery(id+"F15.wireOp",EDGE,"E60.0")])],"isStart":true})});
            var Q14;
            Q14=makeQuery(id+"F16.boolean.opBoolean","COPY",EDGE,{"derivedFrom":makeQuery(id+"F16.opExtrude","CAP_EDGE",EDGE,{"disambiguationData":[OSD([sQuery(id+"F15.wireOp",EDGE,"E63.0")])],"isStart":true})});
            var Q15;
            Q15=makeQuery(id+"F16.boolean.opBoolean","COPY",EDGE,{"derivedFrom":makeQuery(id+"F16.opExtrude","CAP_EDGE",EDGE,{"disambiguationData":[OSD([sQuery(id+"F15.wireOp",EDGE,"E61")])],"isStart":true})});
            var Q16;
            Q16=makeQuery(id+"F16.boolean.opBoolean","COPY",EDGE,{"derivedFrom":makeQuery(id+"F16.opExtrude","CAP_EDGE",EDGE,{"disambiguationData":[OSD([sQuery(id+"F15.wireOp",EDGE,"E60.5")])],"isStart":true})});
            chamfer(context, id + "F27", {"entities" : qUnion([Q0, Q1, Q2, Q3, Q4, Q5, Q6, Q7, Q8, Q9, Q10, Q11, Q12, Q13, Q14, Q15, Q16]), "width" : 0.5 * mm, "tangentPropagation" : true});
        }
    });
